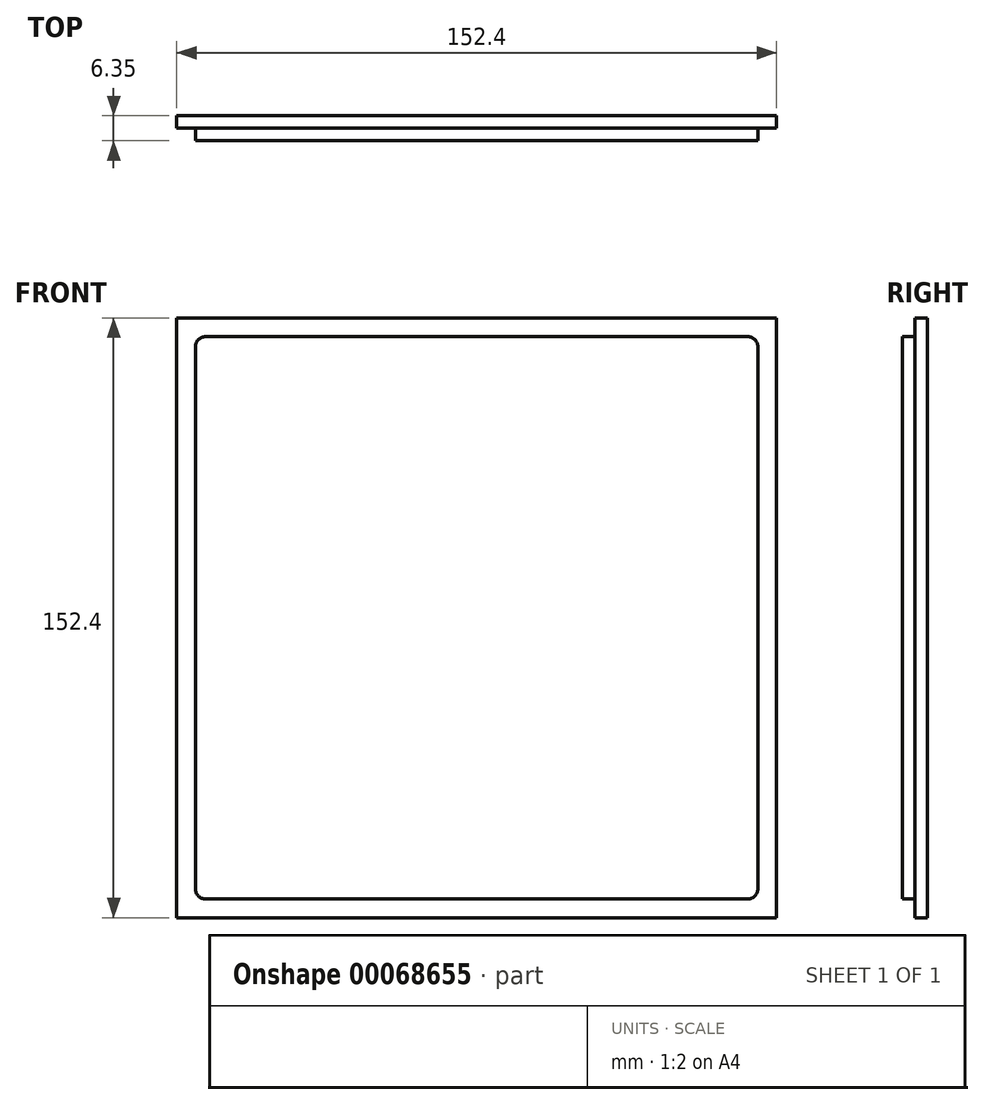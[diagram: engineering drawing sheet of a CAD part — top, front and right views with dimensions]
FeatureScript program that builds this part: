
annotation { "Feature Type Name" : "Feature", "Feature Type Description" : "" }
export const myFeature = defineFeature(function(context is Context, id is Id, definition is map)
    precondition{}
    {
        {
            var Q0;
            Q0=qCreatedBy(makeId("Front.planeOp"),FACE);
            var sketch = newSketch(context, id + "F0", { "sketchPlane" : qUnion([Q0])});
            skLineSegment(sketch, "E0.bottom", {"start": v(0, 0) * mm, "end": v(152.4, 0) * mm});
            skLineSegment(sketch, "E0.top", {"start": v(0, 152.4) * mm, "end": v(152.4, 152.4) * mm});
            skLineSegment(sketch, "E0.left", {"start": v(0, 0) * mm, "end": v(0, 152.4) * mm});
            skLineSegment(sketch, "E0.right", {"start": v(152.4, 0) * mm, "end": v(152.4, 152.4) * mm});
            skSolve(sketch);
        }
        {
            var Q0;
            Q0=makeQuery(id+"F0.imprint","IMPRINT",FACE,{"disambiguationData":[TD([[makeQuery(id+"F0.imprint","IMPRINT",EDGE,{"derivedFrom":sQuery(id+"F0.wireOp",EDGE,"E0.bottom")}),1.0]])]});
            extrude(context, id + "F1", {"entities" : qUnion([Q0]), "depth" : 3.17 * mm});
        }
        {
            var Q0;
            Q0=makeQuery(id+"F1.opExtrude","CAP_FACE",FACE,{"disambiguationData":[OSD([sQuery(id+"F0.wireOp",EDGE,"E0.bottom"),sQuery(id+"F0.wireOp",EDGE,"E0.top"),sQuery(id+"F0.wireOp",EDGE,"E0.left"),sQuery(id+"F0.wireOp",EDGE,"E0.right")])],"isStart":false});
            var sketch = newSketch(context, id + "F2", { "sketchPlane" : qUnion([Q0])});
            skLineSegment(sketch, "E1.bottom", {"start": v(7.3, 147.64) * mm, "end": v(145.1, 147.64) * mm});
            skLineSegment(sketch, "E1.top", {"start": v(7.3, 4.76) * mm, "end": v(145.1, 4.76) * mm});
            skLineSegment(sketch, "E1.left", {"start": v(4.76, 145.1) * mm, "end": v(4.76, 7.3) * mm});
            skLineSegment(sketch, "E1.right", {"start": v(147.64, 145.1) * mm, "end": v(147.64, 7.3) * mm});
            skPoint(sketch, "E2.visualSharp", {"position": v(4.76, 147.64) * mm});
            skArc(sketch, "E2.filletArc", {"start": v(7.3, 147.64) * mm, "mid": v(5.5, 146.9) * mm, "end": v(4.76, 145.1) * mm});
            skPoint(sketch, "E3.visualSharp", {"position": v(147.64, 147.64) * mm});
            skArc(sketch, "E3.filletArc", {"start": v(147.64, 145.1) * mm, "mid": v(146.9, 146.9) * mm, "end": v(145.1, 147.64) * mm});
            skPoint(sketch, "E4.visualSharp", {"position": v(147.64, 4.76) * mm});
            skArc(sketch, "E4.filletArc", {"start": v(145.1, 4.76) * mm, "mid": v(146.9, 5.5) * mm, "end": v(147.64, 7.3) * mm});
            skPoint(sketch, "E5.visualSharp", {"position": v(4.76, 4.76) * mm});
            skArc(sketch, "E5.filletArc", {"start": v(4.76, 7.3) * mm, "mid": v(5.5, 5.5) * mm, "end": v(7.3, 4.76) * mm});
            skSolve(sketch);
        }
        {
            var Q0;
            Q0=makeQuery(id+"F2.imprint","IMPRINT",FACE,{"disambiguationData":[TD([[makeQuery(id+"F2.imprint","IMPRINT",EDGE,{"derivedFrom":sQuery(id+"F2.wireOp",EDGE,"E1.bottom")}),-1.0]])]});
            extrude(context, id + "F3", {"entities" : qUnion([Q0]), "operationType" : NewBodyOperationType.ADD, "depth" : 3.17 * mm});
        }
    });
